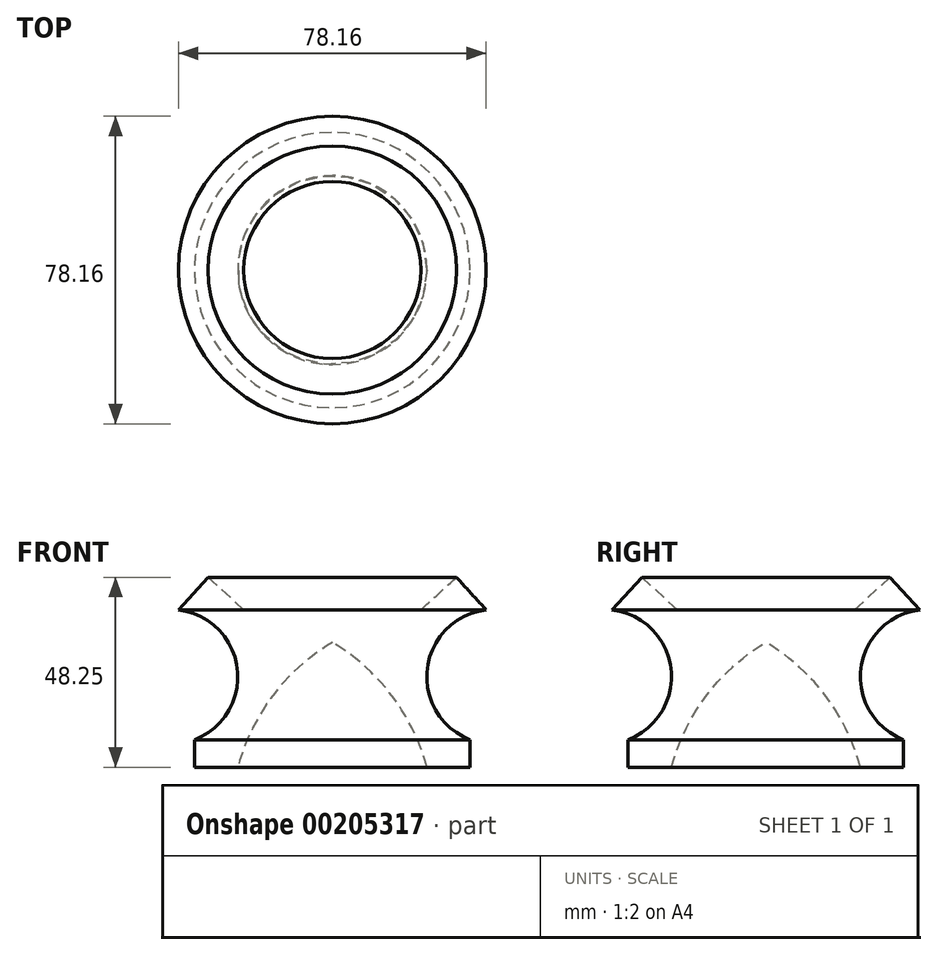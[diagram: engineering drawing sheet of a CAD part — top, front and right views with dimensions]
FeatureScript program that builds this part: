
annotation { "Feature Type Name" : "Feature", "Feature Type Description" : "" }
export const myFeature = defineFeature(function(context is Context, id is Id, definition is map)
    precondition{}
    {
        {
            var Q0;
            Q0=qCreatedBy(makeId("Front.planeOp"),FACE);
            var sketch = newSketch(context, id + "F0", { "sketchPlane" : qUnion([Q0])});
            skLineSegment(sketch, "E0", {"start": v(0, 0) * mm, "end": v(-35, 0) * mm});
            skLineSegment(sketch, "E1", {"start": v(0, 40) * mm, "end": v(-22.5, 40) * mm});
            skLineSegment(sketch, "E2", {"start": v(-22.5, 40) * mm, "end": v(-31.55, 48.25) * mm});
            skLineSegment(sketch, "E3", {"start": v(-31.55, 48.25) * mm, "end": v(-39.08, 40) * mm});
            skLineSegment(sketch, "E4", {"start": v(-35, 0) * mm, "end": v(-35, 7) * mm});
            skArc(sketch, "E5", {"start": v(-35, 7) * mm, "mid": v(-24.13, 25.1) * mm, "end": v(-39.08, 40) * mm});
            skArc(sketch, "E6", {"start": v(0, 31.72) * mm, "mid": v(-15.12, 18.22) * mm, "end": v(-24, 0) * mm});
            skLineSegment(sketch, "E7", {"start": v(0, 40) * mm, "end": v(0, 31.72) * mm});
            skLineSegment(sketch, "E8", {"start": v(0, 31.72) * mm, "end": v(0, 0) * mm, "construction": true});
            skSolve(sketch);
        }
        {
            var Q0;
            Q0=makeQuery(id+"F0.imprint","IMPRINT",FACE,{"disambiguationData":[TD([[makeQuery(id+"F0.imprint","IMPRINT",EDGE,{"derivedFrom":sQuery(id+"F0.wireOp",EDGE,"E1")}),1.0]])]});
            var Q1;
            Q1=sQuery(id+"F0.wireOp",EDGE,"E8");
            revolve(context, id + "F1", {"entities" : qUnion([Q0]), "axis" : qUnion([Q1]), "revolveType" : RevolveType.FULL});
        }
    });
